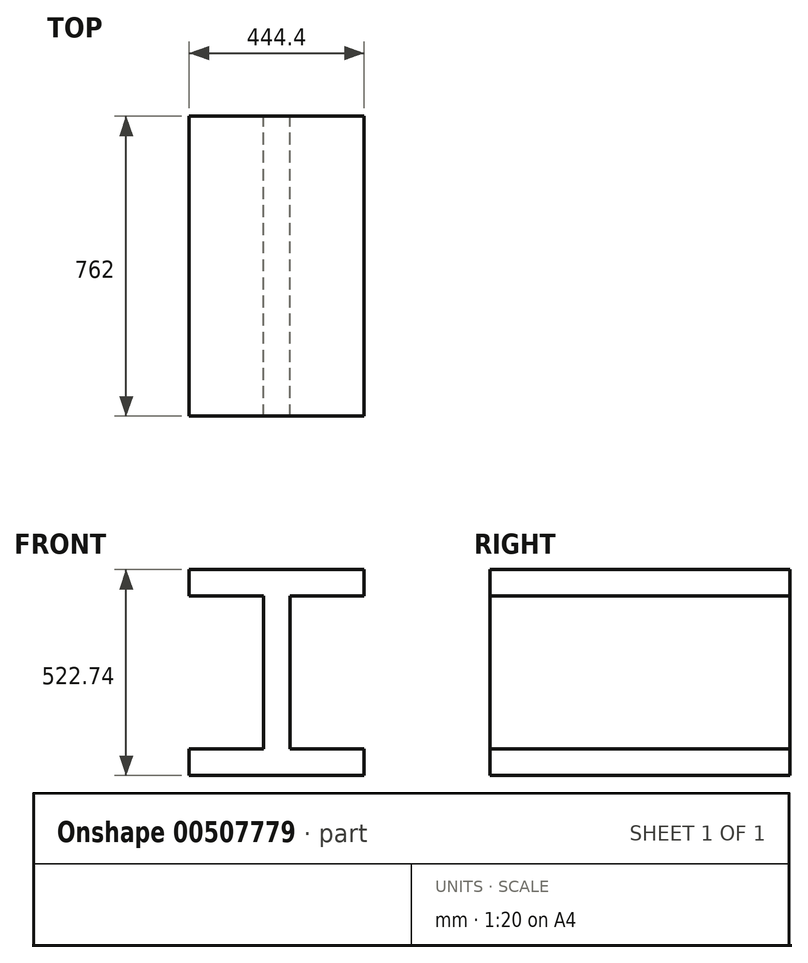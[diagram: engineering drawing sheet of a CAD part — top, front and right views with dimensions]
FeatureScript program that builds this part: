
annotation { "Feature Type Name" : "Feature", "Feature Type Description" : "" }
export const myFeature = defineFeature(function(context is Context, id is Id, definition is map)
    precondition{}
    {
        {
            var Q0;
            Q0=qCreatedBy(makeId("Front.planeOp"),FACE);
            var sketch = newSketch(context, id + "F0", { "sketchPlane" : qUnion([Q0])});
            skLineSegment(sketch, "E0", {"start": v(0, 0) * mm, "end": v(0, 279.4) * mm, "construction": true});
            skLineSegment(sketch, "E1", {"start": v(0, 0) * mm, "end": v(-228.6, 0) * mm, "construction": true});
            skLineSegment(sketch, "E2", {"start": v(-33.98, 0) * mm, "end": v(-33.98, 193.8) * mm});
            skLineSegment(sketch, "E3", {"start": v(-33.98, 193.8) * mm, "end": v(-222.2, 193.8) * mm});
            skLineSegment(sketch, "E4", {"start": v(-222.2, 193.8) * mm, "end": v(-222.2, 261.37) * mm});
            skLineSegment(sketch, "E5", {"start": v(-222.2, 261.37) * mm, "end": v(0, 261.37) * mm});
            skLineSegment(sketch, "E6.MirrorCS", {"start": v(222.2, 261.37) * mm, "end": v(0, 261.37) * mm});
            skLineSegment(sketch, "E7.MirrorCS", {"start": v(33.98, 0) * mm, "end": v(33.98, 193.8) * mm});
            skLineSegment(sketch, "E8.MirrorCS", {"start": v(222.2, 193.8) * mm, "end": v(222.2, 261.37) * mm});
            skLineSegment(sketch, "E9.MirrorCS", {"start": v(33.98, 193.8) * mm, "end": v(222.2, 193.8) * mm});
            skLineSegment(sketch, "E10.MirrorCS", {"start": v(33.98, -193.8) * mm, "end": v(222.2, -193.8) * mm});
            skLineSegment(sketch, "E11.MirrorCS", {"start": v(222.2, -193.8) * mm, "end": v(222.2, -261.37) * mm});
            skLineSegment(sketch, "E12.MirrorCS", {"start": v(33.98, 0) * mm, "end": v(33.98, -193.8) * mm});
            skLineSegment(sketch, "E13.MirrorCS", {"start": v(-33.98, -193.8) * mm, "end": v(-222.2, -193.8) * mm});
            skLineSegment(sketch, "E14.MirrorCS", {"start": v(-222.2, -261.37) * mm, "end": v(0, -261.37) * mm});
            skLineSegment(sketch, "E15.MirrorCS", {"start": v(-33.98, 0) * mm, "end": v(-33.98, -193.8) * mm});
            skLineSegment(sketch, "E16.MirrorCS", {"start": v(222.2, -261.37) * mm, "end": v(0, -261.37) * mm});
            skLineSegment(sketch, "E17.MirrorCS", {"start": v(0, 0) * mm, "end": v(0, -279.4) * mm, "construction": true});
            skLineSegment(sketch, "E18.MirrorCS", {"start": v(-222.2, -193.8) * mm, "end": v(-222.2, -261.37) * mm});
            skSolve(sketch);
        }
        {
            var Q0;
            Q0=makeQuery(id+"F0.imprint","IMPRINT",FACE,{"disambiguationData":[TD([[makeQuery(id+"F0.imprint","IMPRINT",EDGE,{"derivedFrom":sQuery(id+"F0.wireOp",EDGE,"E2")}),-1.0]])]});
            extrude(context, id + "F1", {"entities" : qUnion([Q0]), "depth" : 762 * mm});
        }
    });
